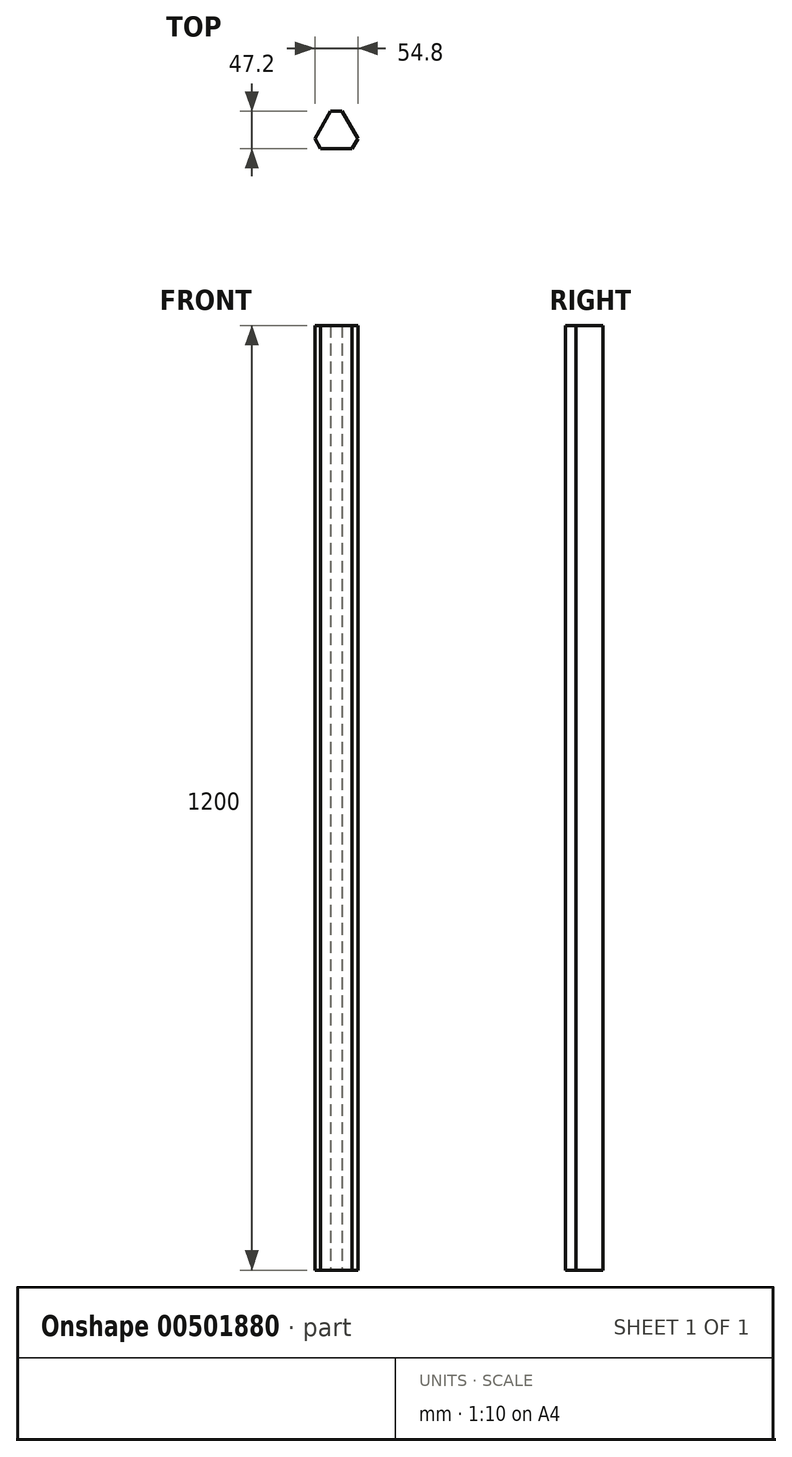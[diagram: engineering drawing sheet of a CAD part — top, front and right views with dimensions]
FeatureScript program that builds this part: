
annotation { "Feature Type Name" : "Feature", "Feature Type Description" : "" }
export const myFeature = defineFeature(function(context is Context, id is Id, definition is map)
    precondition{}
    {
        {
            var Q0;
            Q0=qCreatedBy(makeId("Top.planeOp"),FACE);
            var sketch = newSketch(context, id + "F0", { "sketchPlane" : qUnion([Q0])});
            skLineSegment(sketch, "E0", {"start": v(-7.4, 27.2) * mm, "end": v(7.4, 27.2) * mm});
            skLineSegment(sketch, "E1", {"start": v(-20, -20) * mm, "end": v(20, -20) * mm});
            skLineSegment(sketch, "E2", {"start": v(20, -20) * mm, "end": v(27.4, -7.18) * mm});
            skLineSegment(sketch, "E3.MirrorCS", {"start": v(-20, -20) * mm, "end": v(-27.4, -7.18) * mm});
            skLineSegment(sketch, "E4", {"start": v(7.4, 27.2) * mm, "end": v(27.4, -7.18) * mm});
            skLineSegment(sketch, "E5", {"start": v(-7.4, 27.2) * mm, "end": v(-27.4, -7.18) * mm});
            skSolve(sketch);
        }
        {
            var Q0;
            Q0=makeQuery(id+"F0.imprint","IMPRINT",FACE,{"disambiguationData":[TD([[makeQuery(id+"F0.imprint","IMPRINT",EDGE,{"derivedFrom":sQuery(id+"F0.wireOp",EDGE,"E0")}),-1.0]])]});
            extrude(context, id + "F1", {"entities" : qUnion([Q0]), "depth" : 1200 * mm});
        }
    });
